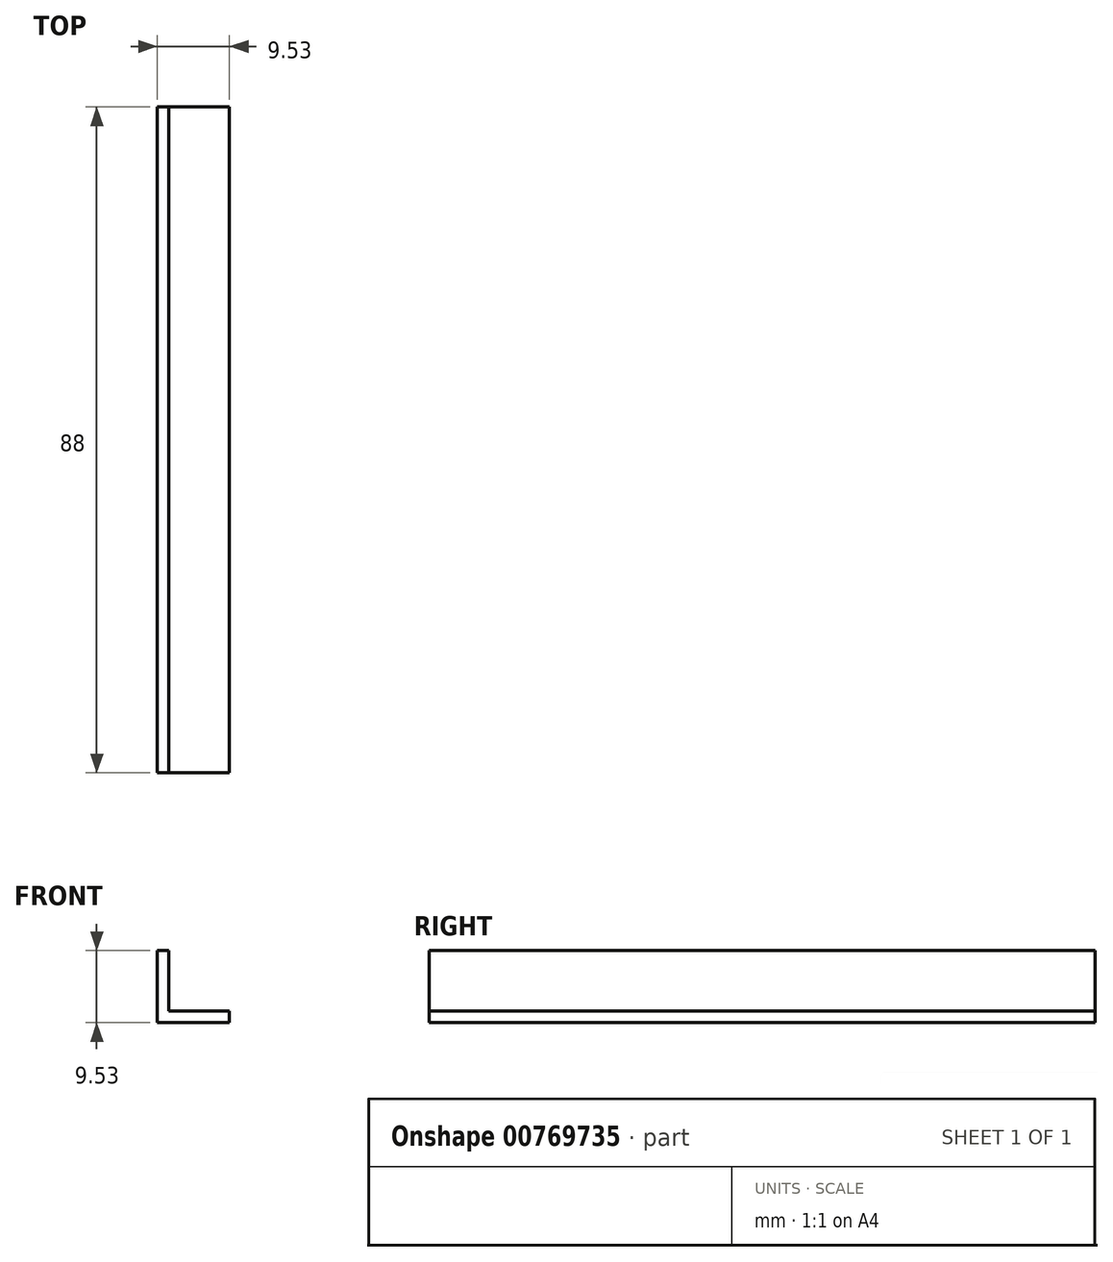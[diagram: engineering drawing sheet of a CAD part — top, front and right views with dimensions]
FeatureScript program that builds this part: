
annotation { "Feature Type Name" : "Feature", "Feature Type Description" : "" }
export const myFeature = defineFeature(function(context is Context, id is Id, definition is map)
    precondition{}
    {
        {
            var Q0;
            Q0=qCreatedBy(makeId("Front.planeOp"),FACE);
            var sketch = newSketch(context, id + "F0", { "sketchPlane" : qUnion([Q0])});
            skLineSegment(sketch, "E0.bottom", {"start": v(0, 0) * mm, "end": v(9.53, 0) * mm});
            skLineSegment(sketch, "E0.top", {"start": v(0, 9.53) * mm, "end": v(9.53, 9.53) * mm});
            skLineSegment(sketch, "E0.left", {"start": v(0, 0) * mm, "end": v(0, 9.53) * mm});
            skLineSegment(sketch, "E0.right", {"start": v(9.53, 0) * mm, "end": v(9.53, 9.53) * mm});
            skSolve(sketch);
        }
        {
            var Q0;
            Q0 = qSketchRegion(id + "F0", true);
            extrude(context, id + "F1", {"entities" : qUnion([Q0]), "depth" : 88 * mm, "offsetDistance" : 25 * mm});
        }
        {
            var Q0;
            Q0=makeQuery(id+"F1.opExtrude","SWEPT_FACE",FACE,{"disambiguationData":[OSD([sQuery(id+"F0.wireOp",EDGE,"E0.right")])]});
            var Q1;
            Q1=makeQuery(id+"F1.opExtrude","CAP_FACE",FACE,{"disambiguationData":[OSD([sQuery(id+"F0.wireOp",EDGE,"E0.bottom"),sQuery(id+"F0.wireOp",EDGE,"E0.top"),sQuery(id+"F0.wireOp",EDGE,"E0.left"),sQuery(id+"F0.wireOp",EDGE,"E0.right")])],"isStart":false});
            var Q2;
            Q2=makeQuery(id+"F1.opExtrude","CAP_FACE",FACE,{"disambiguationData":[OSD([sQuery(id+"F0.wireOp",EDGE,"E0.bottom"),sQuery(id+"F0.wireOp",EDGE,"E0.top"),sQuery(id+"F0.wireOp",EDGE,"E0.left"),sQuery(id+"F0.wireOp",EDGE,"E0.right")])],"isStart":true});
            shell(context, id + "F2", {"entities" : qUnion([Q0, Q1, Q2]), "thickness" : 1.53 * mm});
        }
        {
            var Q0;
            Q0=qCreatedBy(makeId("Front.planeOp"),FACE);
            var sketch = newSketch(context, id + "F3", { "sketchPlane" : qUnion([Q0])});
            skLineSegment(sketch, "E1.bottom", {"start": v(9.53, 9.53) * mm, "end": v(1.53, 9.53) * mm});
            skLineSegment(sketch, "E1.top", {"start": v(9.53, 8) * mm, "end": v(1.53, 8) * mm});
            skLineSegment(sketch, "E1.left", {"start": v(9.53, 9.53) * mm, "end": v(9.53, 8) * mm});
            skLineSegment(sketch, "E1.right", {"start": v(1.53, 9.53) * mm, "end": v(1.53, 8) * mm});
            skSolve(sketch);
        }
        {
            var Q0;
            Q0 = qSketchRegion(id + "F3", true);
            extrude(context, id + "F4", {"entities" : qUnion([Q0]), "operationType" : NewBodyOperationType.REMOVE, "endBound" : BoundingType.THROUGH_ALL, "depth" : 25 * mm, "offsetDistance" : 25 * mm});
        }
    });
